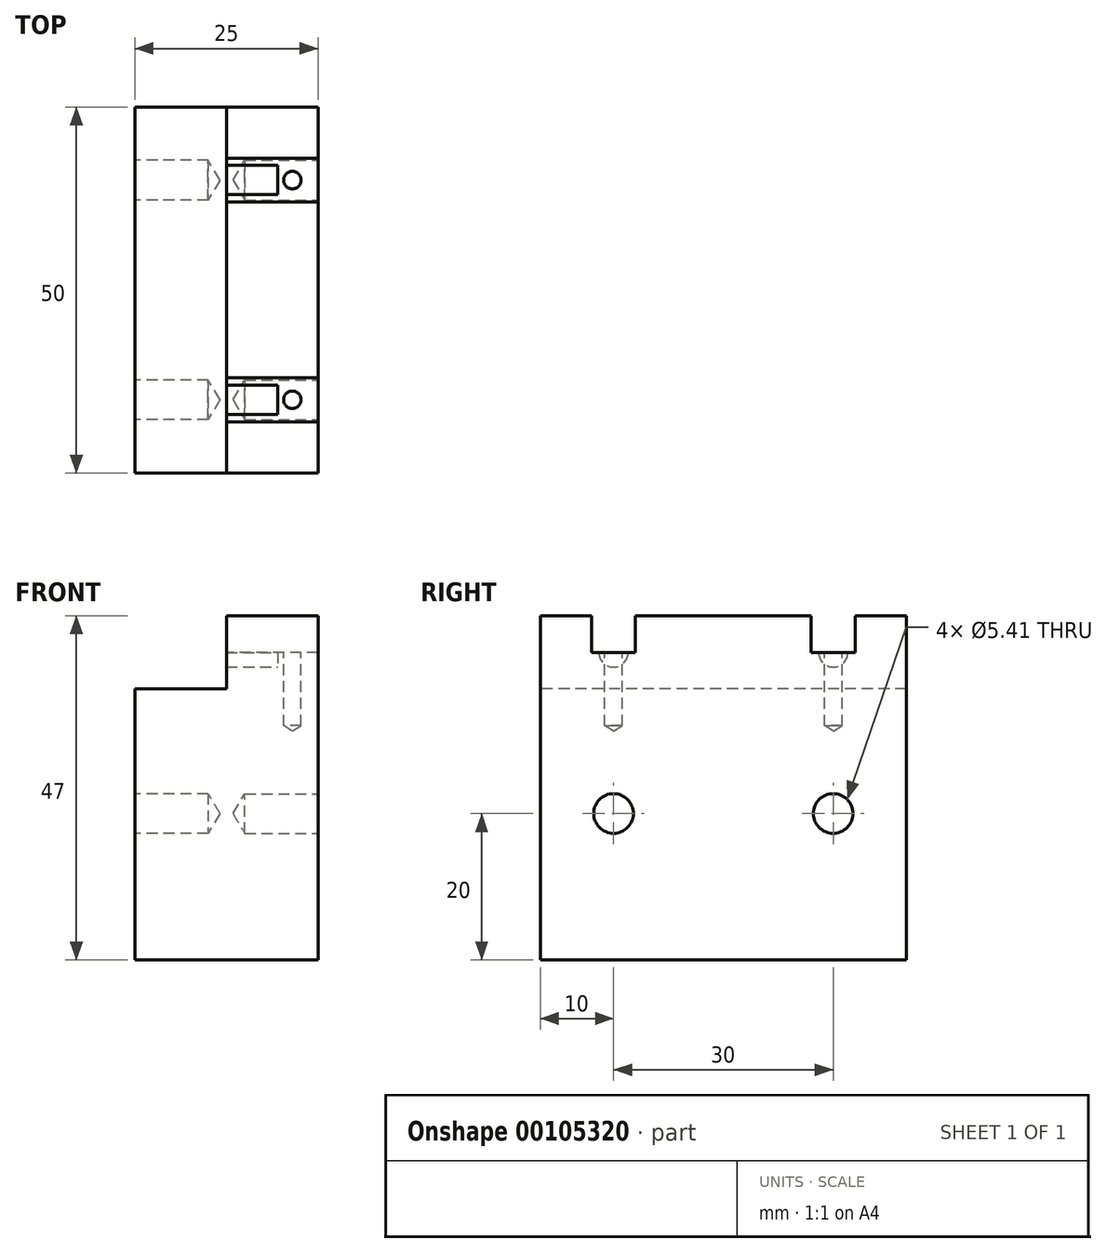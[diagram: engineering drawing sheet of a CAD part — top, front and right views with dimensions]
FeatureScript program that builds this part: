
annotation { "Feature Type Name" : "Feature", "Feature Type Description" : "" }
export const myFeature = defineFeature(function(context is Context, id is Id, definition is map)
    precondition{}
    {
        {
            var Q0;
            Q0=qCreatedBy(makeId("Front.planeOp"),FACE);
            var sketch = newSketch(context, id + "F0", { "sketchPlane" : qUnion([Q0])});
            skLineSegment(sketch, "E0.bottom", {"start": v(-12.5, -20) * mm, "end": v(12.5, -20) * mm});
            skLineSegment(sketch, "E0.top", {"start": v(-12.5, 27) * mm, "end": v(12.5, 27) * mm});
            skLineSegment(sketch, "E0.left", {"start": v(-12.5, -20) * mm, "end": v(-12.5, 27) * mm});
            skLineSegment(sketch, "E0.right", {"start": v(12.5, -20) * mm, "end": v(12.5, 27) * mm});
            skPoint(sketch, "E1", {"position": v(0, -20) * mm});
            skSolve(sketch);
        }
        {
            var Q0;
            Q0=makeQuery(id+"F0.imprint","IMPRINT",FACE,{"disambiguationData":[TD([[makeQuery(id+"F0.imprint","IMPRINT",EDGE,{"derivedFrom":sQuery(id+"F0.wireOp",EDGE,"E0.bottom")}),1.0]])]});
            extrude(context, id + "F1", {"entities" : qUnion([Q0]), "endBound" : BoundingType.SYMMETRIC, "depth" : 50 * mm});
        }
        {
            var Q0;
            Q0=makeQuery(id+"F1.opExtrude","SWEPT_FACE",FACE,{"disambiguationData":[OSD([sQuery(id+"F0.wireOp",EDGE,"E0.left")])]});
            var sketch = newSketch(context, id + "F2", { "sketchPlane" : qUnion([Q0])});
            skPoint(sketch, "E2", {"position": v(15, 0) * mm});
            skLineSegment(sketch, "E3", {"start": v(-30.85, 0) * mm, "end": v(38.37, 0) * mm, "construction": true});
            skLineSegment(sketch, "E4", {"start": v(0, -29.34) * mm, "end": v(0, 34.6) * mm, "construction": true});
            skPoint(sketch, "E4.endSnap0", {"position": v(0, -20) * mm});
            skPoint(sketch, "E5.MirrorP", {"position": v(-15, 0) * mm});
            skSolve(sketch);
        }
        {
            var Q0;
            Q0=makeQuery(id+"F1.opExtrude","SWEPT_FACE",FACE,{"disambiguationData":[OSD([sQuery(id+"F0.wireOp",EDGE,"E0.right")])]});
            var sketch = newSketch(context, id + "F3", { "sketchPlane" : qUnion([Q0])});
            skPoint(sketch, "E6", {"position": v(-15, 0) * mm});
            skLineSegment(sketch, "E7", {"start": v(-44.29, 0) * mm, "end": v(66.43, 0) * mm, "construction": true});
            skLineSegment(sketch, "E8", {"start": v(0, -52.14) * mm, "end": v(0, 55) * mm, "construction": true});
            skPoint(sketch, "E9.MirrorP", {"position": v(15, 0) * mm});
            skSolve(sketch);
        }
        {
            var Q0;
            Q0=sQuery(id+"F2.wireOp",VERTEX,"E5.MirrorP");
            var Q1;
            Q1=sQuery(id+"F2.wireOp",VERTEX,"E2");
            var Q2;
            Q2=sQuery(id+"F3.wireOp",VERTEX,"E6");
            var Q3;
            Q3=sQuery(id+"F3.wireOp",VERTEX,"E9.MirrorP");
            var Q4;
            Q4=makeQuery(id+"F1.opExtrude","SWEPT_BODY",BODY,{"disambiguationData":[OSD([sQuery(id+"F0.wireOp",EDGE,"E0.bottom"),sQuery(id+"F0.wireOp",EDGE,"E0.top"),sQuery(id+"F0.wireOp",EDGE,"E0.left"),sQuery(id+"F0.wireOp",EDGE,"E0.right")])]});
            hole(context, id + "F4", {"style" : HoleStyle.SIMPLE, "endStyle" : HoleEndStyle.BLIND, "standardTappedOrClearance" : lookupTablePath({ "standard" : "ANSI", "engagement" : "75%", "pitch" : "28 tpi", "size" : "1/4", "type" : "Tapped" }), "standardBlindInLast" : lookupTablePath({ "standard" : "ANSI", "engagement" : "75%", "pitch" : "28 tpi", "size" : "1/4", "type" : "Tapped" }), "holeDiameter" : 5.4 * mm, "holeDepth" : 10 * mm, "locations" : qUnion([Q0, Q1, Q2, Q3]), "scope" : qUnion([Q4]), "majorDiameter" : 6.35 * mm});
        }
        {
            var Q0;
            Q0=makeQuery(id+"F1.opExtrude","CAP_FACE",FACE,{"disambiguationData":[OSD([sQuery(id+"F0.wireOp",EDGE,"E0.bottom"),sQuery(id+"F0.wireOp",EDGE,"E0.top"),sQuery(id+"F0.wireOp",EDGE,"E0.left"),sQuery(id+"F0.wireOp",EDGE,"E0.right")])],"isStart":false});
            var sketch = newSketch(context, id + "F5", { "sketchPlane" : qUnion([Q0])});
            skLineSegment(sketch, "E10.bottom", {"start": v(-12.5, 27) * mm, "end": v(0, 27) * mm});
            skLineSegment(sketch, "E10.top", {"start": v(-12.5, 17) * mm, "end": v(0, 17) * mm});
            skLineSegment(sketch, "E10.left", {"start": v(-12.5, 27) * mm, "end": v(-12.5, 17) * mm});
            skLineSegment(sketch, "E10.right", {"start": v(0, 27) * mm, "end": v(0, 17) * mm});
            skLineSegment(sketch, "E11", {"start": v(0, 34.56) * mm, "end": v(0, -4.56) * mm, "construction": true});
            skSolve(sketch);
        }
        {
            var Q0;
            Q0=makeQuery(id+"F5.imprint","IMPRINT",FACE,{"disambiguationData":[TD([[makeQuery(id+"F5.imprint","IMPRINT",EDGE,{"derivedFrom":sQuery(id+"F5.wireOp",EDGE,"E10.bottom")}),-1.0]])]});
            extrude(context, id + "F6", {"entities" : qUnion([Q0]), "operationType" : NewBodyOperationType.REMOVE, "endBound" : BoundingType.THROUGH_ALL, "oppositeDirection" : true, "depth" : 25 * mm});
        }
        {
            var Q0;
            Q0=makeQuery(id+"F1.opExtrude","SWEPT_FACE",FACE,{"disambiguationData":[OSD([sQuery(id+"F0.wireOp",EDGE,"E0.top")])]});
            var sketch = newSketch(context, id + "F7", { "sketchPlane" : qUnion([Q0])});
            skPoint(sketch, "E12", {"position": v(9, 15) * mm});
            skLineSegment(sketch, "E13", {"start": v(-31, 0) * mm, "end": v(25.61, 0) * mm, "construction": true});
            skLineSegment(sketch, "E14", {"start": v(0, -34.4) * mm, "end": v(0, 29.7) * mm, "construction": true});
            skPoint(sketch, "E15.MirrorP", {"position": v(9, -15) * mm});
            skLineSegment(sketch, "E16", {"start": v(-2.92, 15) * mm, "end": v(21.57, 15) * mm, "construction": true});
            skLineSegment(sketch, "E17", {"start": v(-2.92, -15) * mm, "end": v(22.97, -15) * mm, "construction": true});
            skLineSegment(sketch, "E18.bottom", {"start": v(20.1, 12) * mm, "end": v(-2.1, 12) * mm});
            skLineSegment(sketch, "E18.top", {"start": v(20.1, 18) * mm, "end": v(-2.1, 18) * mm});
            skLineSegment(sketch, "E18.left", {"start": v(20.1, 12) * mm, "end": v(20.1, 18) * mm});
            skLineSegment(sketch, "E18.right", {"start": v(-2.1, 12) * mm, "end": v(-2.1, 18) * mm});
            skLineSegment(sketch, "E19.bottom", {"start": v(20.1, -12) * mm, "end": v(-2.1, -12) * mm});
            skLineSegment(sketch, "E19.top", {"start": v(20.1, -18) * mm, "end": v(-2.1, -18) * mm});
            skLineSegment(sketch, "E19.left", {"start": v(20.1, -12) * mm, "end": v(20.1, -18) * mm});
            skLineSegment(sketch, "E19.right", {"start": v(-2.1, -12) * mm, "end": v(-2.1, -18) * mm});
            skSolve(sketch);
        }
        {
            var Q0;
            {var subQ0=sQuery(id+"F7.wireOp",EDGE,"E18.bottom");var subQ1=sQuery(id+"F0.wireOp",EDGE,"E0.top");var subQ2=makeQuery(id+"F1.opExtrude","SWEPT_EDGE",EDGE,{"disambiguationData":[OSD([subQ1,sQuery(id+"F0.wireOp",EDGE,"E0.right")])]});var subQ3=makeQuery(id+"F7.imprint","INTERSECT",VERTEX,{"derivedFrom":[subQ2,subQ0]});Q0=makeQuery(id+"F7.imprint","IMPRINT",FACE,{"disambiguationData":[TD([[makeQuery(id+"F7.imprint","IMPRINT",EDGE,{"disambiguationData":[TD([[subQ3,-1.0]])],"derivedFrom":subQ0}),-1.0]])]});}
            var Q1;
            {var subQ0=sQuery(id+"F7.wireOp",EDGE,"E19.bottom");var subQ1=sQuery(id+"F0.wireOp",EDGE,"E0.top");var subQ2=makeQuery(id+"F1.opExtrude","SWEPT_EDGE",EDGE,{"disambiguationData":[OSD([subQ1,sQuery(id+"F0.wireOp",EDGE,"E0.right")])]});var subQ3=makeQuery(id+"F7.imprint","INTERSECT",VERTEX,{"derivedFrom":[subQ2,subQ0]});Q1=makeQuery(id+"F7.imprint","IMPRINT",FACE,{"disambiguationData":[TD([[makeQuery(id+"F7.imprint","IMPRINT",EDGE,{"disambiguationData":[TD([[subQ3,-1.0]])],"derivedFrom":subQ0}),1.0]])]});}
            extrude(context, id + "F8", {"entities" : qUnion([Q0, Q1]), "operationType" : NewBodyOperationType.REMOVE, "oppositeDirection" : true, "depth" : 5 * mm});
        }
        {
            var Q0;
            Q0=makeQuery(id+"F8.boolean.opBoolean","COPY",FACE,{"derivedFrom":makeQuery(id+"F8.opExtrude","CAP_FACE",FACE,{"disambiguationData":[OSD([sQuery(id+"F0.wireOp",EDGE,"E0.top"),sQuery(id+"F0.wireOp",EDGE,"E0.right"),sQuery(id+"F5.wireOp",EDGE,"E10.bottom"),sQuery(id+"F5.wireOp",EDGE,"E10.right"),sQuery(id+"F7.wireOp",EDGE,"E18.bottom"),sQuery(id+"F7.wireOp",EDGE,"E18.top")])],"isStart":false})});
            var sketch = newSketch(context, id + "F9", { "sketchPlane" : qUnion([Q0])});
            skLineSegment(sketch, "E20", {"start": v(0, 15) * mm, "end": v(15.34, 15) * mm, "construction": true});
            skPoint(sketch, "E20.endSnap0", {"position": v(0, 15) * mm});
            skPoint(sketch, "E21", {"position": v(9, 15) * mm});
            skLineSegment(sketch, "E22.bottom", {"start": v(0, 13) * mm, "end": v(7, 13) * mm});
            skLineSegment(sketch, "E22.top", {"start": v(0, 17) * mm, "end": v(7, 17) * mm});
            skLineSegment(sketch, "E22.left", {"start": v(0, 13) * mm, "end": v(0, 17) * mm});
            skLineSegment(sketch, "E22.right", {"start": v(7, 13) * mm, "end": v(7, 17) * mm});
            skLineSegment(sketch, "E23", {"start": v(0, 15) * mm, "end": v(7, 15) * mm});
            skSolve(sketch);
        }
        {
            var Q0;
            Q0=makeQuery(id+"F8.boolean.opBoolean","COPY",FACE,{"derivedFrom":makeQuery(id+"F8.opExtrude","CAP_FACE",FACE,{"disambiguationData":[OSD([sQuery(id+"F0.wireOp",EDGE,"E0.top"),sQuery(id+"F0.wireOp",EDGE,"E0.right"),sQuery(id+"F5.wireOp",EDGE,"E10.bottom"),sQuery(id+"F5.wireOp",EDGE,"E10.right"),sQuery(id+"F7.wireOp",EDGE,"E19.bottom"),sQuery(id+"F7.wireOp",EDGE,"E19.top")])],"isStart":false})});
            var sketch = newSketch(context, id + "F10", { "sketchPlane" : qUnion([Q0])});
            skLineSegment(sketch, "E24", {"start": v(0, -15) * mm, "end": v(14.48, -15) * mm, "construction": true});
            skPoint(sketch, "E25", {"position": v(9, -15) * mm});
            skLineSegment(sketch, "E26.bottom", {"start": v(0, -13) * mm, "end": v(7, -13) * mm});
            skLineSegment(sketch, "E26.top", {"start": v(0, -17) * mm, "end": v(7, -17) * mm});
            skLineSegment(sketch, "E26.left", {"start": v(0, -13) * mm, "end": v(0, -17) * mm});
            skLineSegment(sketch, "E26.right", {"start": v(7, -13) * mm, "end": v(7, -17) * mm});
            skLineSegment(sketch, "E27", {"start": v(0, -15) * mm, "end": v(7.24, -15) * mm});
            skSolve(sketch);
        }
        {
            var Q0;
            Q0=sQuery(id+"F9.wireOp",VERTEX,"E21");
            var Q1;
            Q1=sQuery(id+"F10.wireOp",VERTEX,"E25");
            var Q2;
            Q2=makeQuery(id+"F1.opExtrude","SWEPT_BODY",BODY,{"disambiguationData":[OSD([sQuery(id+"F0.wireOp",EDGE,"E0.bottom"),sQuery(id+"F0.wireOp",EDGE,"E0.top"),sQuery(id+"F0.wireOp",EDGE,"E0.left"),sQuery(id+"F0.wireOp",EDGE,"E0.right")])]});
            hole(context, id + "F11", {"style" : HoleStyle.SIMPLE, "endStyle" : HoleEndStyle.BLIND, "standardTappedOrClearance" : lookupTablePath({ "standard" : "ISO", "engagement" : "75%", "pitch" : "0.6 mm", "size" : "M3", "type" : "Tapped" }), "standardBlindInLast" : lookupTablePath({ "standard" : "ISO", "engagement" : "75%", "pitch" : "0.6 mm", "size" : "M3", "type" : "Tapped" }), "holeDiameter" : 2.4 * mm, "holeDepth" : 10 * mm, "locations" : qUnion([Q0, Q1]), "scope" : qUnion([Q2])});
        }
        {
            var Q0;
            {var subQ0=sQuery(id+"F9.wireOp",EDGE,"E22.top");Q0=makeQuery(id+"F9.imprint","IMPRINT",FACE,{"disambiguationData":[TD([[makeQuery(id+"F9.imprint","IMPRINT",EDGE,{"derivedFrom":subQ0}),-1.0]])]});}
            var Q1;
            Q1=sQuery(id+"F9.wireOp",EDGE,"E20");
            revolve(context, id + "F12", {"operationType" : NewBodyOperationType.REMOVE, "entities" : qUnion([Q0]), "axis" : qUnion([Q1]), "revolveType" : RevolveType.FULL, "oppositeDirection" : true});
        }
        {
            var Q0;
            {var subQ0=sQuery(id+"F10.wireOp",EDGE,"E26.bottom");Q0=makeQuery(id+"F10.imprint","IMPRINT",FACE,{"disambiguationData":[TD([[makeQuery(id+"F10.imprint","IMPRINT",EDGE,{"derivedFrom":subQ0}),-1.0]])]});}
            var Q1;
            Q1=sQuery(id+"F10.wireOp",EDGE,"E24");
            revolve(context, id + "F13", {"operationType" : NewBodyOperationType.REMOVE, "entities" : qUnion([Q0]), "axis" : qUnion([Q1]), "revolveType" : RevolveType.FULL, "oppositeDirection" : true});
        }
    });
